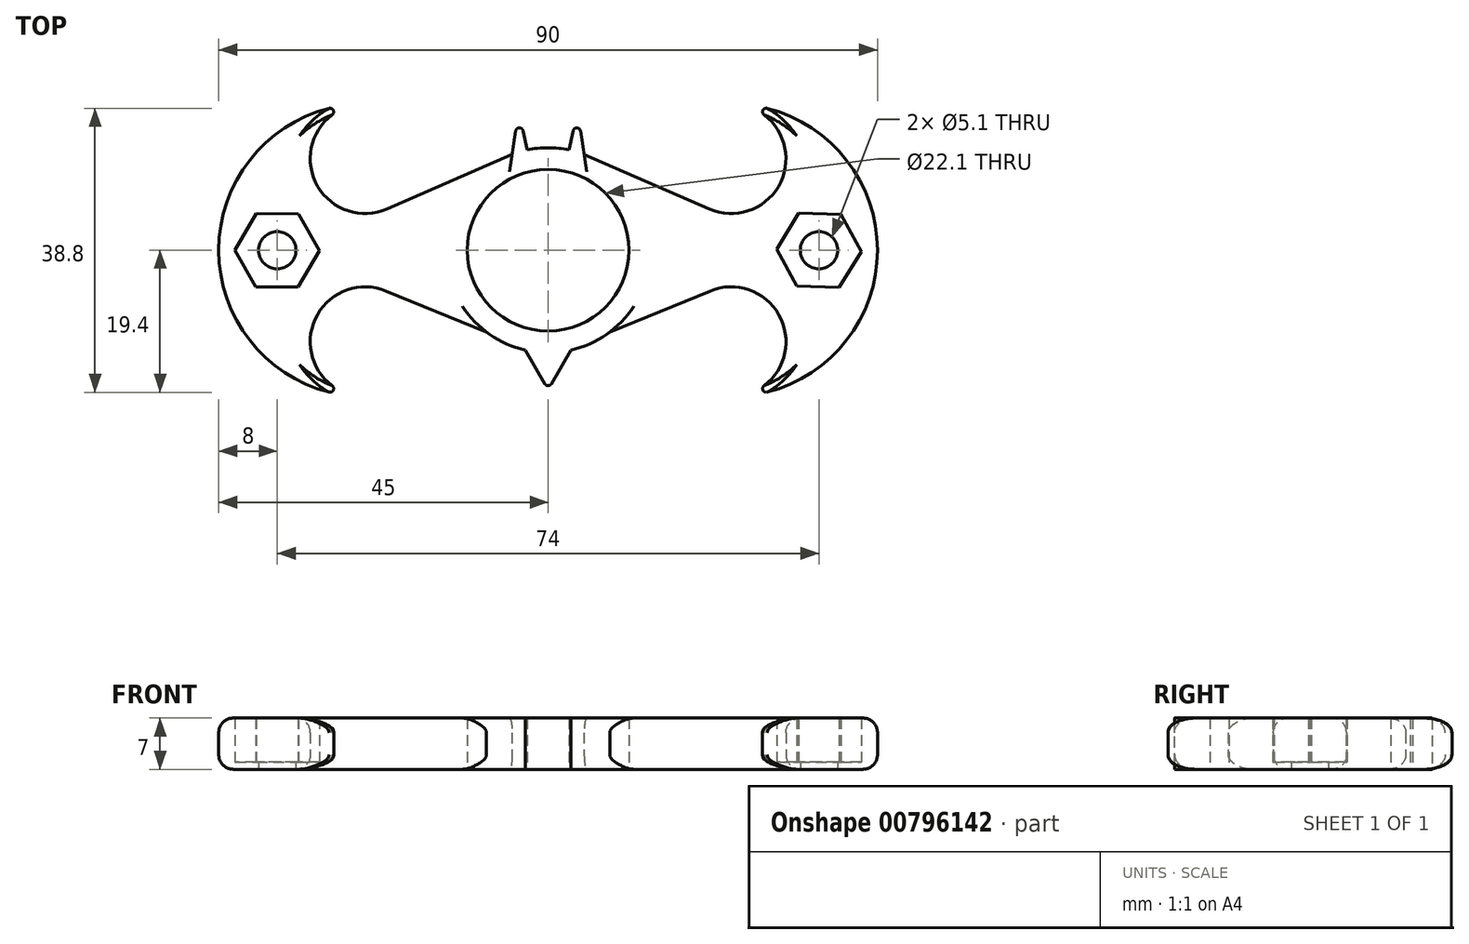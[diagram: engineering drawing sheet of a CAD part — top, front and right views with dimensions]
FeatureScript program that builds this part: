
annotation { "Feature Type Name" : "Feature", "Feature Type Description" : "" }
export const myFeature = defineFeature(function(context is Context, id is Id, definition is map)
    precondition{}
    {
        {
            var Q0;
            Q0=qCreatedBy(makeId("Top.planeOp"),FACE);
            var sketch = newSketch(context, id + "F0", { "sketchPlane" : qUnion([Q0])});
            skCircle(sketch, "E0", {"center": v(-7.5, 4.5) * mm, "radius": 11.05 * mm});
            skLineSegment(sketch, "E1", {"start": v(-7.5, 4.5) * mm, "end": v(-7.5, 56.04) * mm, "construction": true});
            skLineSegment(sketch, "E2", {"start": v(-7.5, 4.5) * mm, "end": v(-59.04, 4.5) * mm, "construction": true});
            skLineSegment(sketch, "E3", {"start": v(-7.5, 4.5) * mm, "end": v(44.04, 4.5) * mm, "construction": true});
            skCircle(sketch, "E4", {"center": v(-7.5, 4.5) * mm, "radius": 35 * mm, "construction": true});
            skPoint(sketch, "E5", {"position": v(-42.5, 4.5) * mm});
            skPoint(sketch, "E6", {"position": v(27.5, 4.5) * mm});
            skPoint(sketch, "E7", {"position": v(-7.5, 39.5) * mm});
            skCircle(sketch, "E8", {"center": v(-7.5, 4.5) * mm, "radius": 25 * mm, "construction": true});
            skPoint(sketch, "E9", {"position": v(-7.5, 29.5) * mm});
            skPoint(sketch, "E10", {"position": v(17.5, 4.5) * mm});
            skPoint(sketch, "E11", {"position": v(-32.5, 4.5) * mm});
            skLineSegment(sketch, "E12", {"start": v(-32.5, 4.5) * mm, "end": v(-32.5, 29.5) * mm, "construction": true});
            skLineSegment(sketch, "E13", {"start": v(-32.5, 4.5) * mm, "end": v(-32.5, -20.5) * mm, "construction": true});
            skLineSegment(sketch, "E14", {"start": v(17.5, 4.5) * mm, "end": v(17.5, -20.5) * mm, "construction": true});
            skLineSegment(sketch, "E15", {"start": v(17.5, 4.5) * mm, "end": v(17.5, 29.5) * mm, "construction": true});
            skLineSegment(sketch, "E16", {"start": v(-7.5, 29.5) * mm, "end": v(17.5, 29.5) * mm, "construction": true});
            skLineSegment(sketch, "E17", {"start": v(-7.5, 29.5) * mm, "end": v(-32.5, 29.5) * mm, "construction": true});
            skPoint(sketch, "E18", {"position": v(-32.5, 17) * mm});
            skPoint(sketch, "E19", {"position": v(-32.5, -8) * mm});
            skPoint(sketch, "E20", {"position": v(-20, 29.5) * mm});
            skPoint(sketch, "E21", {"position": v(5, 29.5) * mm});
            skPoint(sketch, "E22", {"position": v(17.5, 17) * mm});
            skPoint(sketch, "E23", {"position": v(17.5, -8) * mm});
            skCircle(sketch, "E24", {"center": v(-7.5, 4.5) * mm, "radius": 14 * mm});
            skCircle(sketch, "E25", {"center": v(-32.5, 4.5) * mm, "radius": 20 * mm});
            skCircle(sketch, "E26", {"center": v(17.5, 4.5) * mm, "radius": 20 * mm});
            skCircle(sketch, "E27", {"center": v(-32.5, 17) * mm, "radius": 7.5 * mm});
            skCircle(sketch, "E28", {"center": v(-32.5, -8) * mm, "radius": 7.5 * mm});
            skCircle(sketch, "E29", {"center": v(17.5, -8) * mm, "radius": 7.5 * mm});
            skCircle(sketch, "E30", {"center": v(17.5, 17) * mm, "radius": 7.5 * mm});
            skPoint(sketch, "E31", {"position": v(-7.5, 18.5) * mm});
            skPoint(sketch, "E32", {"position": v(-11.5, 23.5) * mm});
            skPoint(sketch, "E33", {"position": v(-3.5, 23.5) * mm});
            skLineSegment(sketch, "E34", {"start": v(-12.42, 17.6) * mm, "end": v(-11.5, 23.5) * mm});
            skLineSegment(sketch, "E35", {"start": v(-2.58, 17.6) * mm, "end": v(-3.5, 23.5) * mm});
            skLineSegment(sketch, "E36", {"start": v(-11.5, 23.5) * mm, "end": v(-7.5, 4.5) * mm});
            skLineSegment(sketch, "E37", {"start": v(-3.5, 23.5) * mm, "end": v(-7.5, 4.5) * mm});
            skPoint(sketch, "E38", {"position": v(-44.5, 4.5) * mm});
            skCircle(sketch, "E39.cCircle", {"center": v(-44.5, 4.5) * mm, "radius": 5 * mm, "construction": true});
            skLineSegment(sketch, "E39.0", {"start": v(-38.73, 4.47) * mm, "end": v(-41.64, -0.52) * mm});
            skLineSegment(sketch, "E39.1", {"start": v(-41.64, -0.52) * mm, "end": v(-47.41, -0.48) * mm});
            skLineSegment(sketch, "E39.2", {"start": v(-47.41, -0.48) * mm, "end": v(-50.27, 4.53) * mm});
            skLineSegment(sketch, "E39.3", {"start": v(-50.27, 4.53) * mm, "end": v(-47.36, 9.52) * mm});
            skLineSegment(sketch, "E39.4", {"start": v(-47.36, 9.52) * mm, "end": v(-41.59, 9.48) * mm});
            skLineSegment(sketch, "E39.5", {"start": v(-41.59, 9.48) * mm, "end": v(-38.73, 4.47) * mm});
            skPoint(sketch, "E39.0.midPoint", {"position": v(-40.18, 1.98) * mm});
            skPoint(sketch, "E40", {"position": v(29.5, 4.5) * mm});
            skCircle(sketch, "E41.cCircle", {"center": v(29.5, 4.5) * mm, "radius": 5 * mm, "construction": true});
            skLineSegment(sketch, "E41.0", {"start": v(35.27, 4.34) * mm, "end": v(32.25, -0.58) * mm});
            skLineSegment(sketch, "E41.1", {"start": v(32.25, -0.58) * mm, "end": v(26.48, -0.42) * mm});
            skLineSegment(sketch, "E41.2", {"start": v(26.48, -0.42) * mm, "end": v(23.73, 4.66) * mm});
            skLineSegment(sketch, "E41.3", {"start": v(23.73, 4.66) * mm, "end": v(26.75, 9.58) * mm});
            skLineSegment(sketch, "E41.4", {"start": v(26.75, 9.58) * mm, "end": v(32.52, 9.42) * mm});
            skLineSegment(sketch, "E41.5", {"start": v(32.52, 9.42) * mm, "end": v(35.27, 4.34) * mm});
            skPoint(sketch, "E41.0.midPoint", {"position": v(33.76, 1.88) * mm});
            skPoint(sketch, "E42", {"position": v(-7.5, -14.5) * mm});
            skLineSegment(sketch, "E43", {"start": v(-7.5, -14.5) * mm, "end": v(-18.55, 4.5) * mm});
            skLineSegment(sketch, "E44", {"start": v(-7.5, -14.5) * mm, "end": v(3.55, 4.5) * mm});
            skLineSegment(sketch, "E45", {"start": v(-15.92, -6.68) * mm, "end": v(-29.66, -1.06) * mm});
            skLineSegment(sketch, "E46", {"start": v(0.92, -6.68) * mm, "end": v(14.66, -1.06) * mm});
            skLineSegment(sketch, "E47", {"start": v(-12.42, 17.6) * mm, "end": v(-29.5, 10.13) * mm});
            skLineSegment(sketch, "E48", {"start": v(-2.58, 17.6) * mm, "end": v(14.5, 10.13) * mm});
            skCircle(sketch, "E49", {"center": v(-44.5, 4.5) * mm, "radius": 2.55 * mm});
            skCircle(sketch, "E50", {"center": v(29.5, 4.5) * mm, "radius": 2.55 * mm});
            skSolve(sketch);
        }
        {
            var Q0;
            Q0=makeQuery(id+"F0.imprint","IMPRINT",FACE,{"disambiguationData":[TD([[makeQuery(id+"F0.imprint","IMPRINT",EDGE,{"derivedFrom":sQuery(id+"F0.wireOp",EDGE,"E39.0")}),1.0]])]});
            var Q1;
            {var subQ0=sQuery(id+"F0.wireOp",EDGE,"E43");var subQ1=sQuery(id+"F0.wireOp",EDGE,"E0");var subQ2=makeQuery(id+"F0.imprint","INTERSECT",VERTEX,{"disambiguationData":[OD(1.0)],"derivedFrom":[subQ1,subQ0]});Q1=makeQuery(id+"F0.imprint","IMPRINT",FACE,{"disambiguationData":[TD([[makeQuery(id+"F0.imprint","IMPRINT",EDGE,{"disambiguationData":[TD([[subQ2,-1.0]])],"derivedFrom":subQ1}),-1.0]])]});}
            var Q2;
            {var subQ0=sQuery(id+"F0.wireOp",EDGE,"E25");var subQ1=sQuery(id+"F0.wireOp",EDGE,"E0");var subQ2=makeQuery(id+"F0.imprint","INTERSECT",VERTEX,{"disambiguationData":[OD(1.0)],"derivedFrom":[subQ1,subQ0]});Q2=makeQuery(id+"F0.imprint","IMPRINT",FACE,{"disambiguationData":[TD([[makeQuery(id+"F0.imprint","IMPRINT",EDGE,{"disambiguationData":[TD([[subQ2,-1.0]])],"derivedFrom":subQ1}),-1.0]])]});}
            var Q3;
            {var subQ1=sQuery(id+"F0.wireOp",EDGE,"E0");var subQ6=makeQuery(id+"F0.imprint","INTERSECT",VERTEX,{"disambiguationData":[OD(0.0)],"derivedFrom":[subQ1,sQuery(id+"F0.wireOp",EDGE,"E43")]});Q3=makeQuery(id+"F0.imprint","IMPRINT",FACE,{"disambiguationData":[TD([[makeQuery(id+"F0.imprint","IMPRINT",EDGE,{"disambiguationData":[TD([[subQ6,1.0]])],"derivedFrom":subQ1}),-1.0]])]});}
            var Q4;
            {var subQ1=sQuery(id+"F0.wireOp",EDGE,"E0");var subQ8=sQuery(id+"F0.wireOp",EDGE,"E36");var subQ10=makeQuery(id+"F0.imprint","INTERSECT",VERTEX,{"derivedFrom":[subQ1,subQ8]});Q4=makeQuery(id+"F0.imprint","IMPRINT",FACE,{"disambiguationData":[TD([[makeQuery(id+"F0.imprint","IMPRINT",EDGE,{"disambiguationData":[TD([[subQ10,-1.0]])],"derivedFrom":subQ1}),-1.0]])]});}
            var Q5;
            {var subQ0=sQuery(id+"F0.wireOp",EDGE,"E37");var subQ1=sQuery(id+"F0.wireOp",EDGE,"E0");var subQ2=makeQuery(id+"F0.imprint","INTERSECT",VERTEX,{"derivedFrom":[subQ1,subQ0]});Q5=makeQuery(id+"F0.imprint","IMPRINT",FACE,{"disambiguationData":[TD([[makeQuery(id+"F0.imprint","IMPRINT",EDGE,{"disambiguationData":[TD([[subQ2,-1.0]])],"derivedFrom":subQ1}),-1.0]])]});}
            var Q6;
            {var subQ0=sQuery(id+"F0.wireOp",EDGE,"E34");Q6=makeQuery(id+"F0.imprint","IMPRINT",FACE,{"disambiguationData":[TD([[makeQuery(id+"F0.imprint","IMPRINT",EDGE,{"derivedFrom":subQ0}),-1.0]])]});}
            var Q7;
            {var subQ0=sQuery(id+"F0.wireOp",EDGE,"E35");Q7=makeQuery(id+"F0.imprint","IMPRINT",FACE,{"disambiguationData":[TD([[makeQuery(id+"F0.imprint","IMPRINT",EDGE,{"derivedFrom":subQ0}),1.0]])]});}
            var Q8;
            {var subQ0=sQuery(id+"F0.wireOp",EDGE,"E26");var subQ1=sQuery(id+"F0.wireOp",EDGE,"E0");var subQ2=makeQuery(id+"F0.imprint","INTERSECT",VERTEX,{"disambiguationData":[OD(0.0)],"derivedFrom":[subQ1,subQ0]});Q8=makeQuery(id+"F0.imprint","IMPRINT",FACE,{"disambiguationData":[TD([[makeQuery(id+"F0.imprint","IMPRINT",EDGE,{"disambiguationData":[TD([[subQ2,-1.0]])],"derivedFrom":subQ1}),-1.0]])]});}
            var Q9;
            {var subQ1=sQuery(id+"F0.wireOp",EDGE,"E0");var subQ6=makeQuery(id+"F0.imprint","INTERSECT",VERTEX,{"disambiguationData":[OD(0.0)],"derivedFrom":[subQ1,sQuery(id+"F0.wireOp",EDGE,"E44")]});Q9=makeQuery(id+"F0.imprint","IMPRINT",FACE,{"disambiguationData":[TD([[makeQuery(id+"F0.imprint","IMPRINT",EDGE,{"disambiguationData":[TD([[subQ6,-1.0]])],"derivedFrom":subQ1}),-1.0]])]});}
            var Q10;
            {var subQ0=sQuery(id+"F0.wireOp",EDGE,"E44");var subQ1=sQuery(id+"F0.wireOp",EDGE,"E0");var subQ2=makeQuery(id+"F0.imprint","INTERSECT",VERTEX,{"disambiguationData":[OD(1.0)],"derivedFrom":[subQ1,subQ0]});Q10=makeQuery(id+"F0.imprint","IMPRINT",FACE,{"disambiguationData":[TD([[makeQuery(id+"F0.imprint","IMPRINT",EDGE,{"disambiguationData":[TD([[subQ2,-1.0]])],"derivedFrom":subQ1}),-1.0]])]});}
            var Q11;
            {var subQ0=sQuery(id+"F0.wireOp",EDGE,"E43");var subQ1=sQuery(id+"F0.wireOp",EDGE,"E24");var subQ2=makeQuery(id+"F0.imprint","INTERSECT",VERTEX,{"derivedFrom":[subQ1,subQ0]});Q11=makeQuery(id+"F0.imprint","IMPRINT",FACE,{"disambiguationData":[TD([[makeQuery(id+"F0.imprint","IMPRINT",EDGE,{"disambiguationData":[TD([[subQ2,-1.0]])],"derivedFrom":subQ1}),-1.0]])]});}
            var Q12;
            Q12=makeQuery(id+"F0.imprint","IMPRINT",FACE,{"disambiguationData":[TD([[makeQuery(id+"F0.imprint","IMPRINT",EDGE,{"derivedFrom":sQuery(id+"F0.wireOp",EDGE,"E41.0")}),1.0]])]});
            var Q13;
            {var subQ0=sQuery(id+"F0.wireOp",EDGE,"VWRQcpWG-v6JB-WzOt-1pjG-XEFOC5eGBk41");var subQ1=sQuery(id+"F0.wireOp",EDGE,"E24");var subQ2=makeQuery(id+"F0.imprint","INTERSECT",VERTEX,{"derivedFrom":[subQ1,subQ0]});Q13=makeQuery(id+"F0.imprint","IMPRINT",FACE,{"disambiguationData":[TD([[makeQuery(id+"F0.imprint","IMPRINT",EDGE,{"disambiguationData":[TD([[subQ2,-1.0]])],"derivedFrom":subQ1}),-1.0]])]});}
            var Q14;
            {var subQ0=sQuery(id+"F0.wireOp",EDGE,"EQHGipvJ-TpaZ-PM8R-1l8x-kui38zTTxmQw");var subQ1=sQuery(id+"F0.wireOp",EDGE,"E24");var subQ2=makeQuery(id+"F0.imprint","INTERSECT",VERTEX,{"derivedFrom":[subQ1,subQ0]});Q14=makeQuery(id+"F0.imprint","IMPRINT",FACE,{"disambiguationData":[TD([[makeQuery(id+"F0.imprint","IMPRINT",EDGE,{"disambiguationData":[TD([[subQ2,1.0]])],"derivedFrom":subQ1}),-1.0]])]});}
            extrude(context, id + "F1", {"entities" : qUnion([Q0, Q1, Q2, Q3, Q4, Q5, Q6, Q7, Q8, Q9, Q10, Q11, Q12, Q13, Q14]), "depth" : 7 * mm, "offsetDistance" : 25 * mm});
        }
        {
            var Q0;
            Q0=makeQuery(id+"F1.opExtrude","SWEPT_EDGE",EDGE,{"disambiguationData":[OSD([sQuery(id+"F0.wireOp",EDGE,"E25"),sQuery(id+"F0.wireOp",EDGE,"E28")])]});
            var Q1;
            Q1=makeQuery(id+"F1.opExtrude","SWEPT_EDGE",EDGE,{"disambiguationData":[OSD([sQuery(id+"F0.wireOp",EDGE,"E26"),sQuery(id+"F0.wireOp",EDGE,"E29")])]});
            var Q2;
            Q2=makeQuery(id+"F1.opExtrude","SWEPT_EDGE",EDGE,{"disambiguationData":[OSD([sQuery(id+"F0.wireOp",EDGE,"E26"),sQuery(id+"F0.wireOp",EDGE,"E30")])]});
            var Q3;
            Q3=makeQuery(id+"F1.opExtrude","SWEPT_EDGE",EDGE,{"disambiguationData":[OSD([sQuery(id+"F0.wireOp",EDGE,"E25"),sQuery(id+"F0.wireOp",EDGE,"E27")])]});
            var Q4;
            Q4=makeQuery(id+"F1.opExtrude","SWEPT_EDGE",EDGE,{"disambiguationData":[OSD([sQuery(id+"F0.wireOp",EDGE,"E34"),sQuery(id+"F0.wireOp",EDGE,"E36")])]});
            var Q5;
            Q5=makeQuery(id+"F1.opExtrude","SWEPT_EDGE",EDGE,{"disambiguationData":[OSD([sQuery(id+"F0.wireOp",EDGE,"E35"),sQuery(id+"F0.wireOp",EDGE,"E37")])]});
            var Q6;
            Q6=makeQuery(id+"F1.opExtrude","SWEPT_EDGE",EDGE,{"disambiguationData":[OSD([sQuery(id+"F0.wireOp",EDGE,"E43"),sQuery(id+"F0.wireOp",EDGE,"E44")])]});
            fillet(context, id + "F2", {"entities" : qUnion([Q0, Q1, Q2, Q3, Q4, Q5, Q6]), "radius" : 0.5 * mm, "tangentPropagation" : true, "allowEdgeOverflow" : false});
        }
        {
            var Q0;
            Q0=makeQuery(id+"F1.opExtrude","CAP_EDGE",EDGE,{"disambiguationData":[OSD([sQuery(id+"F0.wireOp",EDGE,"E25")])],"isStart":false});
            var Q1;
            Q1=makeQuery(id+"F1.opExtrude","CAP_EDGE",EDGE,{"disambiguationData":[OSD([sQuery(id+"F0.wireOp",EDGE,"E25")])],"isStart":true});
            var Q2;
            Q2=makeQuery(id+"F1.opExtrude","CAP_EDGE",EDGE,{"disambiguationData":[OSD([sQuery(id+"F0.wireOp",EDGE,"E26")])],"isStart":true});
            var Q3;
            Q3=makeQuery(id+"F1.opExtrude","CAP_EDGE",EDGE,{"disambiguationData":[OSD([sQuery(id+"F0.wireOp",EDGE,"E26")])],"isStart":false});
            fillet(context, id + "F3", {"entities" : qUnion([Q0, Q1, Q2, Q3]), "radius" : 2 * mm, "tangentPropagation" : true, "allowEdgeOverflow" : false});
        }
        {
            var Q0;
            Q0=makeQuery(id+"F0.imprint","IMPRINT",FACE,{"disambiguationData":[TD([[makeQuery(id+"F0.imprint","IMPRINT",EDGE,{"derivedFrom":sQuery(id+"F0.wireOp",EDGE,"E39.0")}),-1.0]])]});
            var Q1;
            Q1=makeQuery(id+"F0.imprint","IMPRINT",FACE,{"disambiguationData":[TD([[makeQuery(id+"F0.imprint","IMPRINT",EDGE,{"derivedFrom":sQuery(id+"F0.wireOp",EDGE,"E41.0")}),-1.0]])]});
            extrude(context, id + "F4", {"entities" : qUnion([Q0, Q1]), "operationType" : NewBodyOperationType.ADD, "depth" : 1 * mm, "offsetDistance" : 25 * mm});
        }
    });
